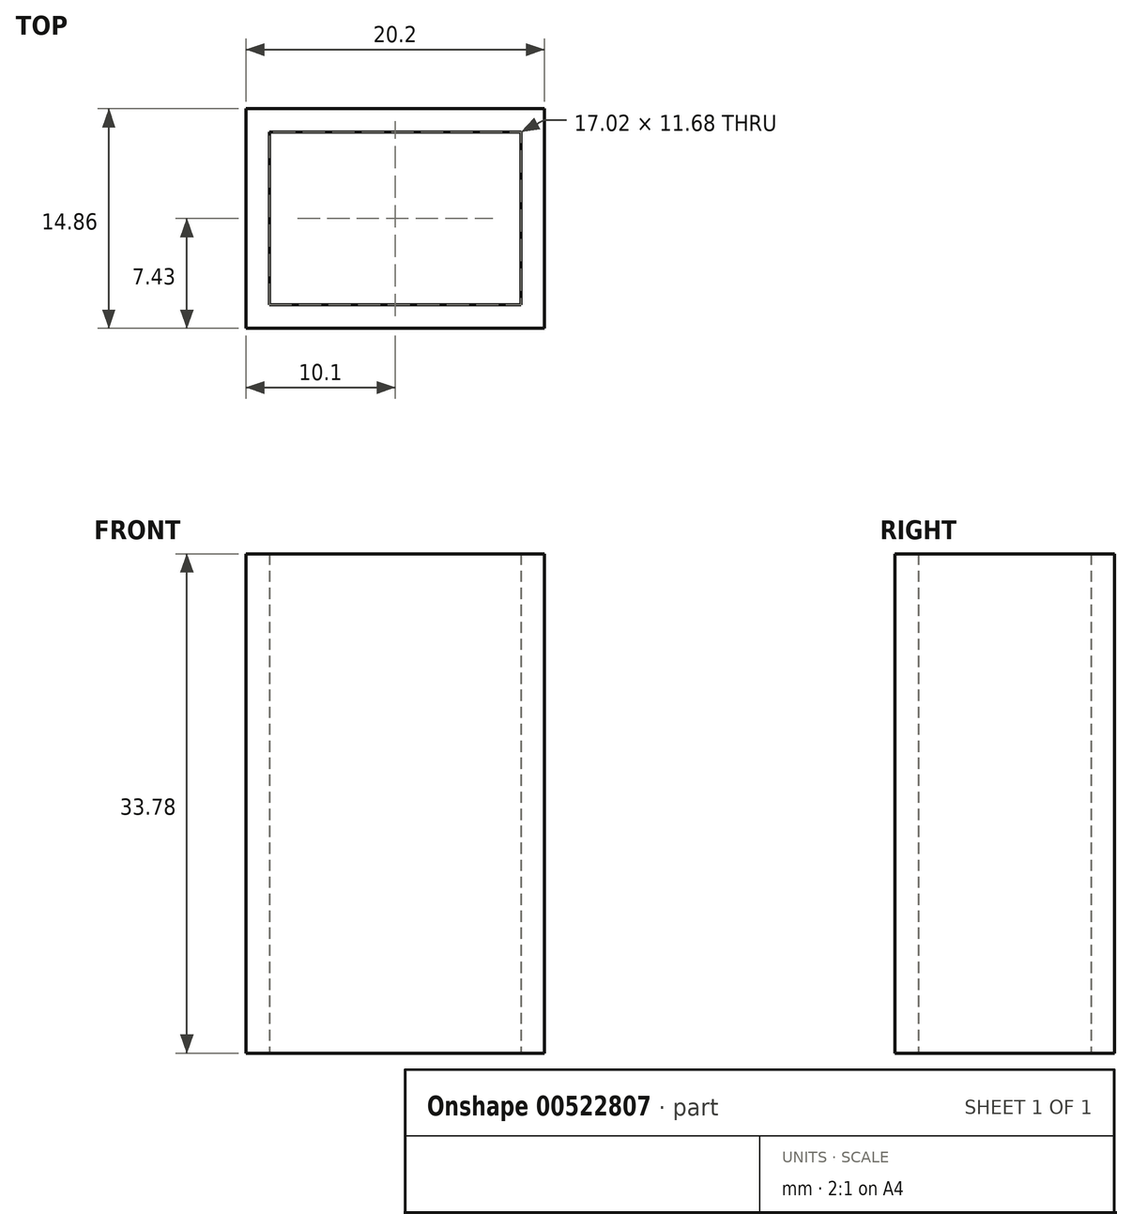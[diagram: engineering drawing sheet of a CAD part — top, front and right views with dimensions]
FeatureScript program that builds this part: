
annotation { "Feature Type Name" : "Feature", "Feature Type Description" : "" }
export const myFeature = defineFeature(function(context is Context, id is Id, definition is map)
    precondition{}
    {
        {
            var Q0;
            Q0=qCreatedBy(makeId("Top.planeOp"),FACE);
            var sketch = newSketch(context, id + "F0", { "sketchPlane" : qUnion([Q0])});
            skLineSegment(sketch, "E0.bottom", {"start": v(8.5, 5.84) * mm, "end": v(-8.5, 5.84) * mm});
            skLineSegment(sketch, "E0.top", {"start": v(8.5, -5.84) * mm, "end": v(-8.5, -5.84) * mm});
            skLineSegment(sketch, "E0.left", {"start": v(8.5, 5.84) * mm, "end": v(8.5, -5.84) * mm});
            skLineSegment(sketch, "E0.right", {"start": v(-8.5, 5.84) * mm, "end": v(-8.5, -5.84) * mm});
            skPoint(sketch, "E0.middle", {"position": v(0, 0) * mm});
            skLineSegment(sketch, "E1.bottom", {"start": v(10.1, 7.43) * mm, "end": v(-10.1, 7.43) * mm});
            skLineSegment(sketch, "E1.top", {"start": v(10.1, -7.43) * mm, "end": v(-10.1, -7.43) * mm});
            skLineSegment(sketch, "E1.left", {"start": v(10.1, 7.43) * mm, "end": v(10.1, -7.43) * mm});
            skLineSegment(sketch, "E1.right", {"start": v(-10.1, 7.43) * mm, "end": v(-10.1, -7.43) * mm});
            skSolve(sketch);
        }
        {
            var Q0;
            Q0 = qSketchRegion(id + "F0", true);
            extrude(context, id + "F1", {"entities" : qUnion([Q0]), "depth" : 33.78 * mm, "offsetDistance" : 25.4 * mm});
        }
    });
